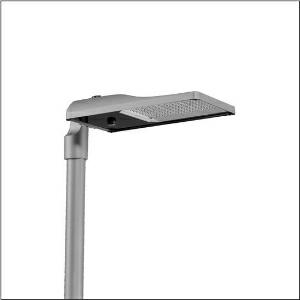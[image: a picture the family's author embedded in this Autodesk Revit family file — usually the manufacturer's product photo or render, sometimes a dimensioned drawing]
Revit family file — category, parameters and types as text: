
# Revit family: streetlight_sl_31_maxi___pl52_5xh8h31t08sa_1c4f
name_source: partatom
category: Lighting Fixtures
units: mm (PartAtom-declared; Revit-internal decimal feet)

## family parameters
Cut with Voids When Loaded = No
Host = Face
Light Source = No
Part Type = Normal
Room Calculation Point = No
Round Connector Dimension = Use Diameter
Shared = No

## types (1)
- --- (1 x LED, 27810 lm, 211.4 W, 3000K)
    Apparent Load = 211 VA
    CIE Flux Codes = 27 59 98 100 100
    Color Rendering = 70
    Color Temperature = 3000K
    Default Elevation = 1800 mm
    Description = Streetlight SL 31 maxi D4i, Desk-Remote mast luminaire for post-top, side-entry; light control with lens of PMMA; light distribution: PL52, direct asymmetric distribution, for standard-compliant lighting for roads and squares; LED: luminous flux: 27.810lm, light colour: 730, colour temperature: 3000K; luminous efficacy: 131,6lm/W; control: pre-setting: logarithmic dimming characteristic, flexible luminous flux parameterisation, time-dependent luminous flux control, constant luminous flux control, power reduction, intelligent temperature release in ECG and LED module, overheat protection; luminaire housing, of diecast aluminium, Siteco® metallic grey (DB 702S), corrosivity category C5 high according to DIN EN ISO 12944; cover of toughened safety glass, transparent, opened without tools; mast flange of diecast aluminium, Siteco® metallic grey (DB 702S), spigot size: 76/60mm, mast flange included unmounted; with cable H07RN-F 2x 1.5mm², cable length: 14,5m, connection cable pre-assembled; mains connection: 220..240V, AC, 50/60Hz; power consumption (at start of service life): 211,4W / (at end of service life): 238W / (with reduced operation 50%): 88,1W; protection rating (complete): IP66; insulation class (complete): insulation class II (safety insulation); impact resistance: IK09; certification: CE, ENEC, ENEC+, VDE, UKCA, ZD4i; permissible operating ambient temperature for outdoor applications: -40..+50°C; packaging unit: 1 piece

Light Distribution: PL52
    Height = 79 mm
    Lamp = 1 x LED
    Lamp Light Flux = 27810 lm
    Lamp Power = 211.4 W
    Lamp count = 1
    Length = 657 mm
    Luminous efficacy = 132 lm/W
    Manufacturer = Siteco
    ModVariant = No
    Model = 5XH8H31T08SA
    Number of Poles = 1
    OnlyDefault = Yes
    Power Factor = 1
    Product Name = Streetlight SL 31 maxi | PL52
    Product group = mast luminaire | pylon top
    ProductGroupID = 6100
    Protection Class = Protection class II
    Protection Degree = IP 66
    RLX_Detail_Level = 1
    RLX_Emergency_Light_Flux = 0 lm
    RLX_Emergency_Type = 0
    RLX_Emergency_Type_DB = No
    RlxData = <blob elided: 56773 chars, md5=c4ce7f77>
    Socket = socket
    Standby Power = 0 W
    System Light Flux = 27810 lm
    System Power = 211 W
    Type Comments = factory setting: luminous flux: 100 % | dim-lin: 254 | 727 mA
    Type Image = l_1300303.jpg
    URL = http://relux.com
    VarID = @adj_060377
    Voltage = 0 V
    Weight = 0.00 kg
    Width = 362 mm

## geometry (parser evidence)
native form markers: Blend x4, Sweep x11
no freeform markers — native parametric forms only
